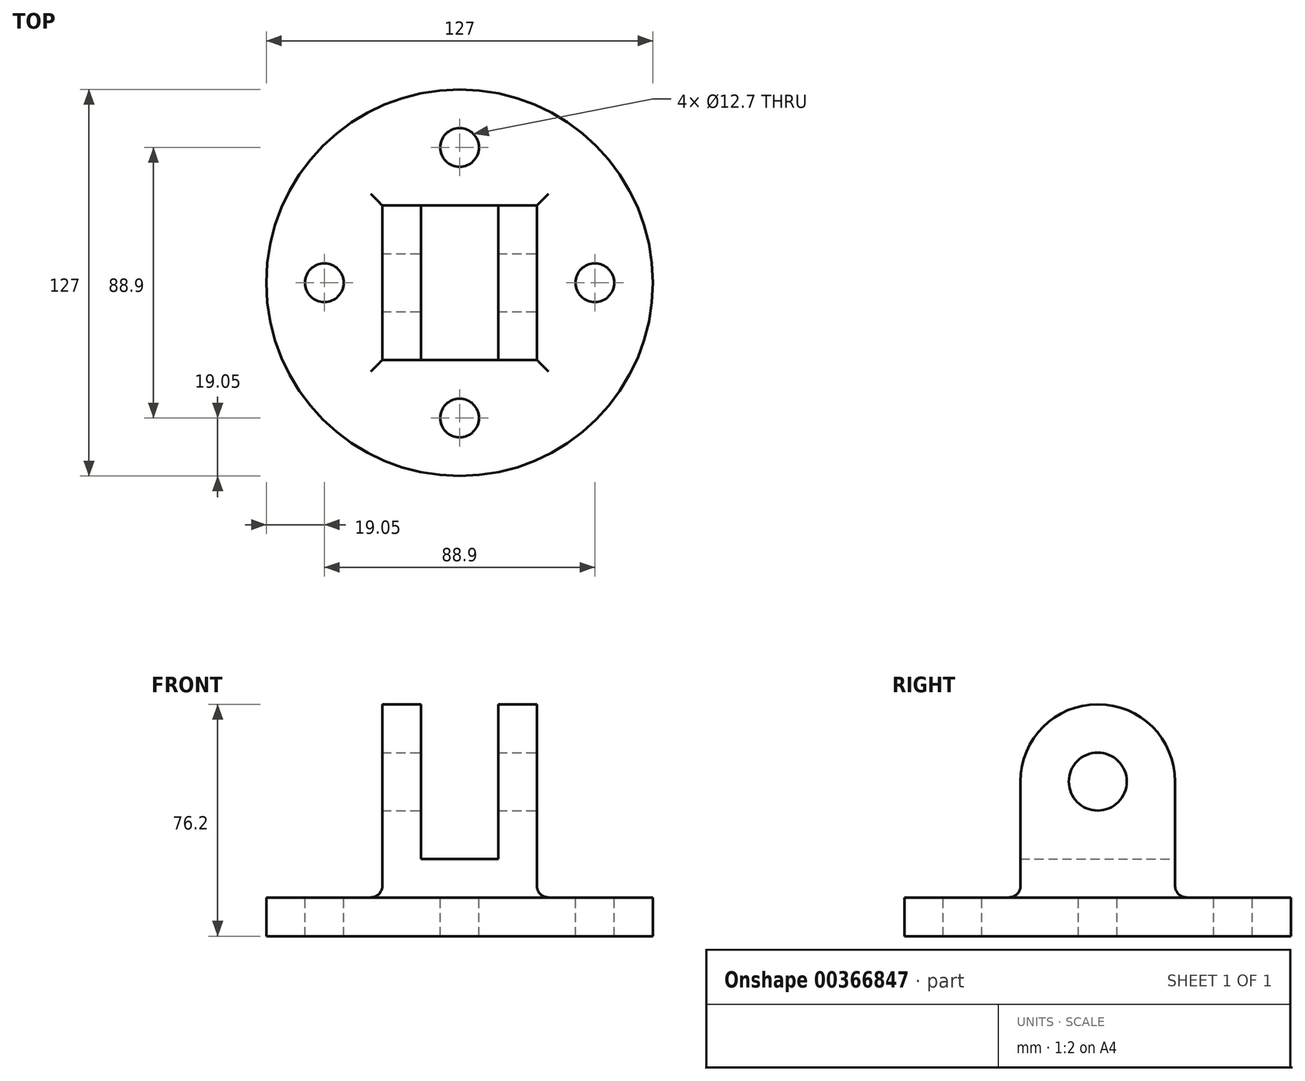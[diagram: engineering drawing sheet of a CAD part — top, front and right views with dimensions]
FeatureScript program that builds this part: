
annotation { "Feature Type Name" : "Feature", "Feature Type Description" : "" }
export const myFeature = defineFeature(function(context is Context, id is Id, definition is map)
    precondition{}
    {
        {
            var Q0;
            Q0=qCreatedBy(makeId("Top.planeOp"),FACE);
            var sketch = newSketch(context, id + "F0", { "sketchPlane" : qUnion([Q0])});
            skCircle(sketch, "E0", {"center": v(0, 0) * mm, "radius": 63.5 * mm});
            skSolve(sketch);
        }
        {
            var Q0;
            Q0 = qSketchRegion(id + "F0", true);
            extrude(context, id + "F1", {"entities" : qUnion([Q0]), "depth" : 12.7 * mm});
        }
        {
            var Q0;
            Q0=qCreatedBy(makeId("Front.planeOp"),FACE);
            var sketch = newSketch(context, id + "F2", { "sketchPlane" : qUnion([Q0])});
            skLineSegment(sketch, "E1", {"start": v(-25.4, 0) * mm, "end": v(-25.4, 50.8) * mm});
            skLineSegment(sketch, "E2", {"start": v(0, 0) * mm, "end": v(-25.4, 0) * mm});
            skLineSegment(sketch, "E3", {"start": v(-25.4, 50.8) * mm, "end": v(-12.7, 50.8) * mm});
            skLineSegment(sketch, "E4", {"start": v(-12.7, 50.8) * mm, "end": v(-12.7, 25.4) * mm});
            skLineSegment(sketch, "E5", {"start": v(-12.7, 25.4) * mm, "end": v(0, 25.4) * mm});
            skLineSegment(sketch, "E6", {"start": v(0, 25.4) * mm, "end": v(0, 0) * mm});
            skLineSegment(sketch, "E7", {"start": v(0, 70.65) * mm, "end": v(0, -42.34) * mm, "construction": true});
            skLineSegment(sketch, "E8.MirrorCS", {"start": v(25.4, 50.8) * mm, "end": v(12.7, 50.8) * mm});
            skLineSegment(sketch, "E9.MirrorCS", {"start": v(12.7, 50.8) * mm, "end": v(12.7, 25.4) * mm});
            skLineSegment(sketch, "E10.MirrorCS", {"start": v(12.7, 25.4) * mm, "end": v(0, 25.4) * mm});
            skLineSegment(sketch, "E11.MirrorCS", {"start": v(25.4, 0) * mm, "end": v(25.4, 50.8) * mm});
            skLineSegment(sketch, "E12.MirrorCS", {"start": v(0, 0) * mm, "end": v(25.4, 0) * mm});
            skSolve(sketch);
        }
        {
            var Q0;
            Q0 = qSketchRegion(id + "F2", true);
            extrude(context, id + "F3", {"entities" : qUnion([Q0]), "operationType" : NewBodyOperationType.ADD, "endBound" : BoundingType.SYMMETRIC, "depth" : 50.8 * mm});
        }
        {
            var Q0;
            Q0=makeQuery(id+"F3.opExtrude","SWEPT_FACE",FACE,{"disambiguationData":[OSD([sQuery(id+"F2.wireOp",EDGE,"E11.MirrorCS")])]});
            cPlane(context, id + "F4", {"entities" : qUnion([Q0]), "cplaneType" : CPlaneType.OFFSET, "offset" : 0 * mm, "width" : 152.4 * mm, "height" : 152.4 * mm});
        }
        {
            var Q0;
            Q0=qCreatedBy(id+"F4.planeOp",FACE);
            var sketch = newSketch(context, id + "F5", { "sketchPlane" : qUnion([Q0])});
            skArc(sketch, "E13", {"start": v(25.4, 50.8) * mm, "mid": v(0, 76.2) * mm, "end": v(-25.4, 50.8) * mm});
            skLineSegment(sketch, "E14", {"start": v(-25.4, 50.8) * mm, "end": v(25.4, 50.8) * mm});
            skSolve(sketch);
        }
        {
            var Q0;
            Q0 = qSketchRegion(id + "F5", true);
            extrude(context, id + "F6", {"entities" : qUnion([Q0]), "operationType" : NewBodyOperationType.ADD, "oppositeDirection" : true, "depth" : 12.7 * mm});
        }
        {
            var Q0;
            Q0=makeQuery(id+"F3.opExtrude","SWEPT_FACE",FACE,{"disambiguationData":[OSD([sQuery(id+"F2.wireOp",EDGE,"E1")])]});
            cPlane(context, id + "F7", {"entities" : qUnion([Q0]), "cplaneType" : CPlaneType.OFFSET, "offset" : 0 * mm, "width" : 152.4 * mm, "height" : 152.4 * mm});
        }
        {
            var Q0;
            Q0=qCreatedBy(id+"F7.planeOp",FACE);
            var sketch = newSketch(context, id + "F8", { "sketchPlane" : qUnion([Q0])});
            skArc(sketch, "E15", {"start": v(25.4, 50.8) * mm, "mid": v(0, 76.2) * mm, "end": v(-25.4, 50.8) * mm});
            skLineSegment(sketch, "E16", {"start": v(-25.4, 50.8) * mm, "end": v(25.4, 50.8) * mm});
            skSolve(sketch);
        }
        {
            var Q0;
            Q0 = qSketchRegion(id + "F8", true);
            extrude(context, id + "F9", {"entities" : qUnion([Q0]), "operationType" : NewBodyOperationType.ADD, "oppositeDirection" : true, "depth" : 12.7 * mm});
        }
        {
            var Q0;
            Q0=makeQuery(id+"F6.boolean.opBoolean","MERGE",FACE,{"derivedFrom":[makeQuery(id+"F3.opExtrude","SWEPT_FACE",FACE,{"disambiguationData":[OSD([sQuery(id+"F2.wireOp",EDGE,"E11.MirrorCS")])]}),makeQuery(id+"F6.opExtrude","CAP_FACE",FACE,{"disambiguationData":[OSD([sQuery(id+"F5.wireOp",EDGE,"E13"),sQuery(id+"F5.wireOp",EDGE,"E14")])],"isStart":true})]});
            var sketch = newSketch(context, id + "F10", { "sketchPlane" : qUnion([Q0])});
            skCircle(sketch, "E17", {"center": v(0, 50.8) * mm, "radius": 9.53 * mm});
            skSolve(sketch);
        }
        {
            var Q0;
            Q0 = qSketchRegion(id + "F10", true);
            extrude(context, id + "F11", {"entities" : qUnion([Q0]), "operationType" : NewBodyOperationType.REMOVE, "endBound" : BoundingType.THROUGH_ALL, "oppositeDirection" : true, "depth" : 25.4 * mm});
        }
        {
            var Q0;
            Q0=makeQuery(id+"F1.opExtrude","CAP_FACE",FACE,{"disambiguationData":[OSD([sQuery(id+"F0.wireOp",EDGE,"E0")])],"isStart":false});
            var sketch = newSketch(context, id + "F12", { "sketchPlane" : qUnion([Q0])});
            skCircle(sketch, "E18", {"center": v(0, 44.45) * mm, "radius": 6.35 * mm});
            skCircle(sketch, "E19", {"center": v(44.45, 0) * mm, "radius": 6.35 * mm});
            skCircle(sketch, "E20", {"center": v(0, -44.45) * mm, "radius": 6.35 * mm});
            skCircle(sketch, "E21", {"center": v(-44.45, 0) * mm, "radius": 6.35 * mm});
            skSolve(sketch);
        }
        {
            var Q0;
            Q0 = qSketchRegion(id + "F12", true);
            extrude(context, id + "F13", {"entities" : qUnion([Q0]), "operationType" : NewBodyOperationType.REMOVE, "endBound" : BoundingType.THROUGH_ALL, "oppositeDirection" : true, "depth" : 25.4 * mm});
        }
        {
            var Q0;
            Q0=makeQuery(id+"F3.boolean.opBoolean","INTERSECT",EDGE,{"derivedFrom":[makeQuery(id+"F1.opExtrude","CAP_FACE",FACE,{"disambiguationData":[OSD([sQuery(id+"F0.wireOp",EDGE,"E0")])],"isStart":false}),makeQuery(id+"F3.opExtrude","SWEPT_FACE",FACE,{"disambiguationData":[OSD([sQuery(id+"F2.wireOp",EDGE,"E1")])]})]});
            var Q1;
            Q1=makeQuery(id+"F3.boolean.opBoolean","INTERSECT",EDGE,{"derivedFrom":[makeQuery(id+"F1.opExtrude","CAP_FACE",FACE,{"disambiguationData":[OSD([sQuery(id+"F0.wireOp",EDGE,"E0")])],"isStart":false}),makeQuery(id+"F3.opExtrude","CAP_FACE",FACE,{"disambiguationData":[OSD([sQuery(id+"F2.wireOp",EDGE,"E1"),sQuery(id+"F2.wireOp",EDGE,"E2"),sQuery(id+"F2.wireOp",EDGE,"E3"),sQuery(id+"F2.wireOp",EDGE,"E4"),sQuery(id+"F2.wireOp",EDGE,"E5"),sQuery(id+"F2.wireOp",EDGE,"E8.MirrorCS"),sQuery(id+"F2.wireOp",EDGE,"E9.MirrorCS"),sQuery(id+"F2.wireOp",EDGE,"E10.MirrorCS"),sQuery(id+"F2.wireOp",EDGE,"E11.MirrorCS"),sQuery(id+"F2.wireOp",EDGE,"E12.MirrorCS")])],"isStart":false})]});
            var Q2;
            Q2=makeQuery(id+"F3.boolean.opBoolean","INTERSECT",EDGE,{"derivedFrom":[makeQuery(id+"F1.opExtrude","CAP_FACE",FACE,{"disambiguationData":[OSD([sQuery(id+"F0.wireOp",EDGE,"E0")])],"isStart":false}),makeQuery(id+"F3.opExtrude","SWEPT_FACE",FACE,{"disambiguationData":[OSD([sQuery(id+"F2.wireOp",EDGE,"E11.MirrorCS")])]})]});
            var Q3;
            Q3=makeQuery(id+"F3.boolean.opBoolean","INTERSECT",EDGE,{"derivedFrom":[makeQuery(id+"F1.opExtrude","CAP_FACE",FACE,{"disambiguationData":[OSD([sQuery(id+"F0.wireOp",EDGE,"E0")])],"isStart":false}),makeQuery(id+"F3.opExtrude","CAP_FACE",FACE,{"disambiguationData":[OSD([sQuery(id+"F2.wireOp",EDGE,"E1"),sQuery(id+"F2.wireOp",EDGE,"E2"),sQuery(id+"F2.wireOp",EDGE,"E3"),sQuery(id+"F2.wireOp",EDGE,"E4"),sQuery(id+"F2.wireOp",EDGE,"E5"),sQuery(id+"F2.wireOp",EDGE,"E8.MirrorCS"),sQuery(id+"F2.wireOp",EDGE,"E9.MirrorCS"),sQuery(id+"F2.wireOp",EDGE,"E10.MirrorCS"),sQuery(id+"F2.wireOp",EDGE,"E11.MirrorCS"),sQuery(id+"F2.wireOp",EDGE,"E12.MirrorCS")])],"isStart":true})]});
            fillet(context, id + "F14", {"entities" : qUnion([Q0, Q1, Q2, Q3]), "radius" : 3.8 * mm, "tangentPropagation" : true, "allowEdgeOverflow" : false});
        }
    });
